# Revit family: revitupgrade
name_source: partatom
category: Furniture
units: mm (PartAtom-declared; Revit-internal decimal feet)

## family parameters
Always vertical = Yes
Cut with Voids When Loaded = No
Enable Cutting in Views = No
Render Appearance Source = Family Geometry
Room Calculation Point = No
Shared = No
Work Plane-Based = No

## types (9) — shared parameters
Assembly Code = E2020200
Caster = Steelcase - 6205 Black
Default Elevation = 0.00 mm
Description = Building on best-in-class ergonomics, Series 2 introduces additional performance features and fresh new style choices for personalisation, expanding one of our most popular office chair collections.
Manufacturer = Steelcase
Release Date = October 2024
URL = https://www.steelcase.com

## per-type parameters (varying)
| type | Coathanger | Headrest | Style Number(s) | Upholstery Back |
| Air | No | No | 436AIR,436AIRCN | No |
| Air 3D | No | No | 436AIR3D,436AIR3DCN | Yes |
| Upholstered | No | No | 436UPH,436UPHCN | Yes |
| Air - Coathanger | Yes | No | 436AIR,436AIRCN | No |
| Air - Headrest | No | Yes | 436AIR,436AIRCN | No |
| Air 3D - Coathanger | Yes | No | 436AIR3D,436AIR3DCN | Yes |
| Air 3D - Headrest | No | Yes | 436AIR3D,436AIR3DCN | Yes |
| Upholstered - Coathanger | Yes | No | 436UPH,436UPHCN | Yes |
| Upholstered - Headrest | No | Yes | 436UPH,436UPHCN | Yes |

## geometry (parser evidence)
native form markers: Sweep x8
no freeform markers — native parametric forms only
